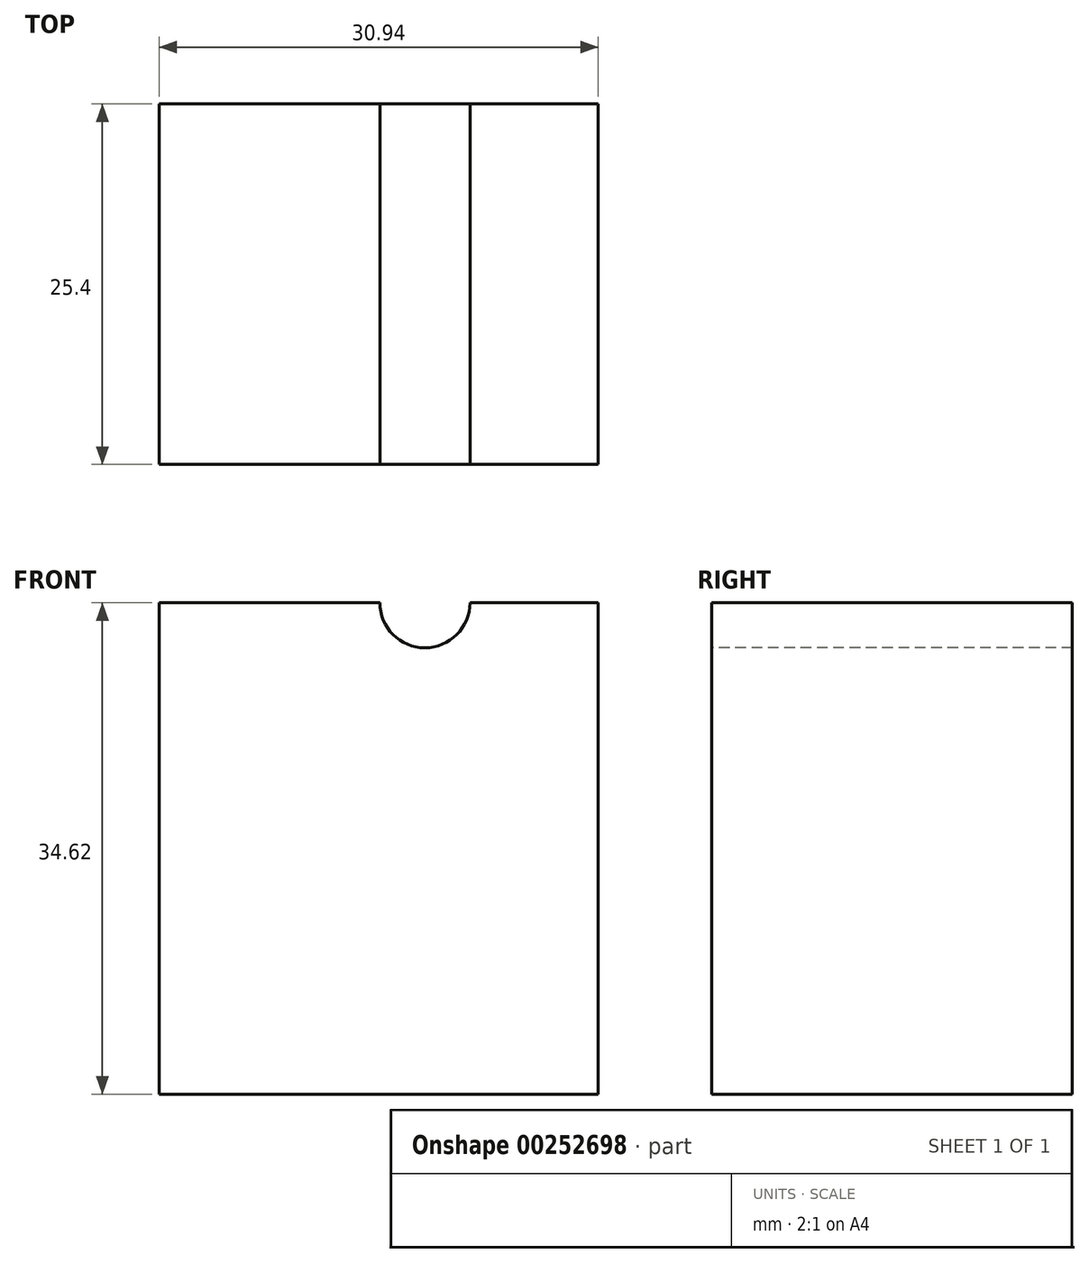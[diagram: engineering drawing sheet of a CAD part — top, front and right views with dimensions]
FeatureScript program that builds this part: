
annotation { "Feature Type Name" : "Feature", "Feature Type Description" : "" }
export const myFeature = defineFeature(function(context is Context, id is Id, definition is map)
    precondition{}
    {
        {
            var Q0;
            Q0=qCreatedBy(makeId("Front.planeOp"),FACE);
            var sketch = newSketch(context, id + "F0", { "sketchPlane" : qUnion([Q0])});
            skLineSegment(sketch, "E0.bottom", {"start": v(0, 0) * mm, "end": v(30.94, 0) * mm});
            skLineSegment(sketch, "E0.top", {"start": v(0, 34.62) * mm, "end": v(30.94, 34.62) * mm});
            skLineSegment(sketch, "E0.left", {"start": v(0, 0) * mm, "end": v(0, 34.62) * mm});
            skLineSegment(sketch, "E0.right", {"start": v(30.94, 0) * mm, "end": v(30.94, 34.62) * mm});
            skSolve(sketch);
        }
        {
            var Q0;
            Q0 = qSketchRegion(id + "F0", true);
            extrude(context, id + "F1", {"entities" : qUnion([Q0]), "depth" : 25.4 * mm});
        }
        {
            var Q0;
            Q0=makeQuery(id+"F1.opExtrude","CAP_FACE",FACE,{"disambiguationData":[OSD([sQuery(id+"F0.wireOp",EDGE,"E0.bottom"),sQuery(id+"F0.wireOp",EDGE,"E0.top"),sQuery(id+"F0.wireOp",EDGE,"E0.left"),sQuery(id+"F0.wireOp",EDGE,"E0.right")])],"isStart":false});
            var sketch = newSketch(context, id + "F2", { "sketchPlane" : qUnion([Q0])});
            skPoint(sketch, "E1", {"position": v(9.93, 34.62) * mm});
            skPoint(sketch, "E2", {"position": v(18.72, 34.62) * mm});
            skPoint(sketch, "E3", {"position": v(9.75, 35.21) * mm});
            skPoint(sketch, "E4", {"position": v(26.37, 34.62) * mm});
            skPoint(sketch, "E5", {"position": v(2.22, 86.86) * mm});
            skSolve(sketch);
        }
        {
            var Q0;
            Q0=sQuery(id+"F2.wireOp",VERTEX,"E2");
            var Q1;
            Q1=makeQuery(id+"F1.opExtrude","SWEPT_BODY",BODY,{"disambiguationData":[OSD([sQuery(id+"F0.wireOp",EDGE,"E0.bottom"),sQuery(id+"F0.wireOp",EDGE,"E0.top"),sQuery(id+"F0.wireOp",EDGE,"E0.left"),sQuery(id+"F0.wireOp",EDGE,"E0.right")])]});
            hole(context, id + "F3", {"style" : HoleStyle.SIMPLE, "endStyle" : HoleEndStyle.THROUGH, "holeDiameter" : 6.35 * mm, "tappedDepth" : 12.7 * mm, "tapClearance" : 3, "locations" : qUnion([Q0]), "scope" : qUnion([Q1])});
        }
    });
